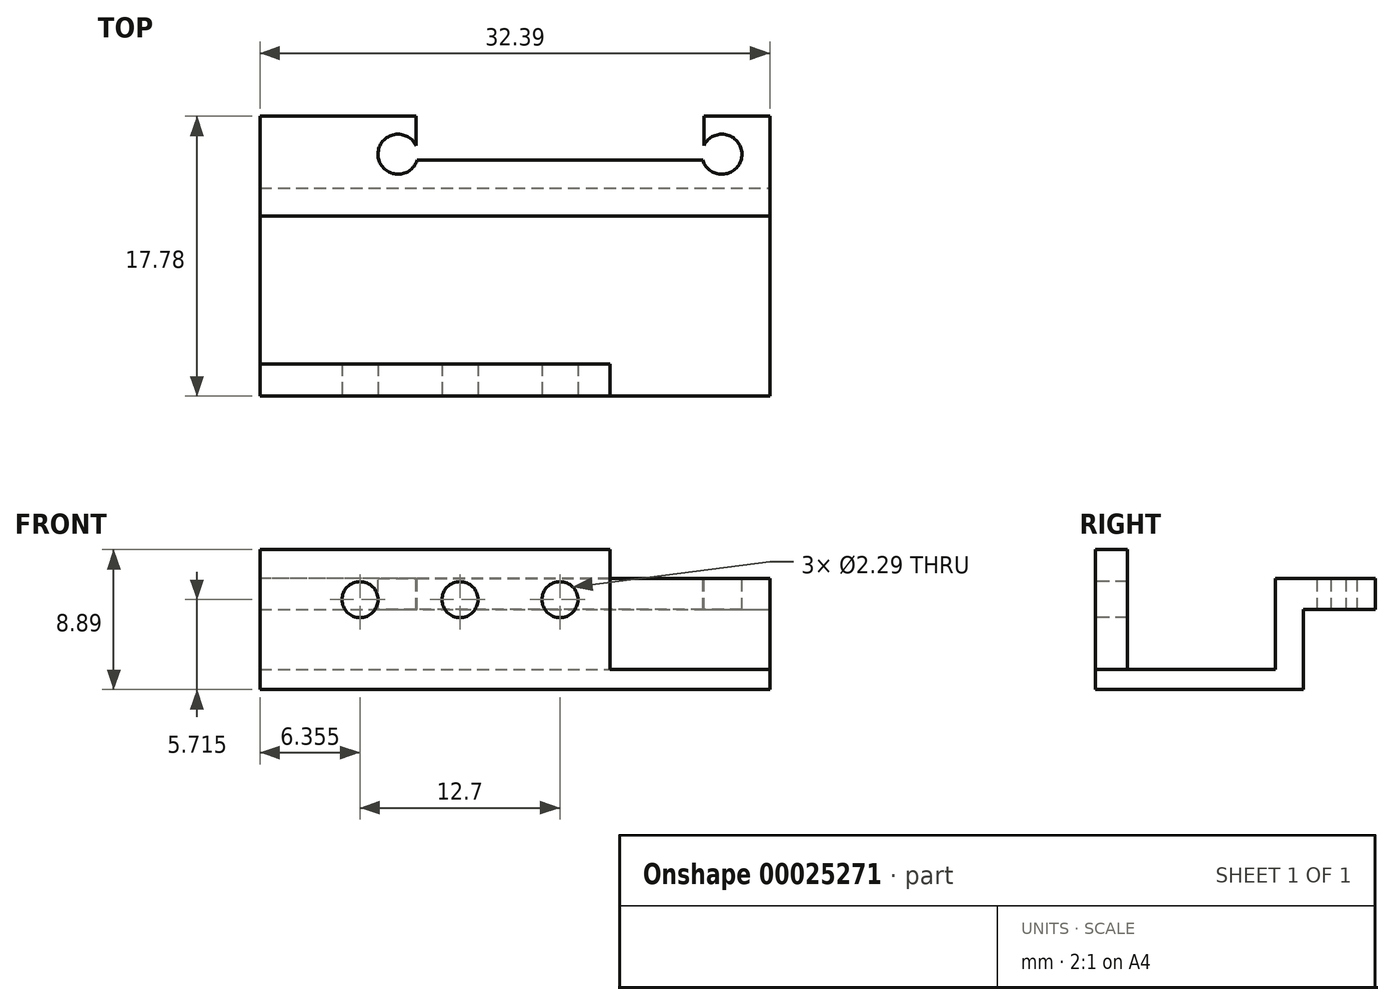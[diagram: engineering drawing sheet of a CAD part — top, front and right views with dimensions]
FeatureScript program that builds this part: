
annotation { "Feature Type Name" : "Feature", "Feature Type Description" : "" }
export const myFeature = defineFeature(function(context is Context, id is Id, definition is map)
    precondition{}
    {
        {
            var Q0;
            Q0=qCreatedBy(makeId("Front.planeOp"),FACE);
            var sketch = newSketch(context, id + "F0", { "sketchPlane" : qUnion([Q0])});
            skLineSegment(sketch, "E0.bottom", {"start": v(0, 0) * mm, "end": v(-22.23, 0) * mm});
            skLineSegment(sketch, "E0.top", {"start": v(0, 8.9) * mm, "end": v(-22.23, 8.89) * mm});
            skLineSegment(sketch, "E0.left", {"start": v(0, 0) * mm, "end": v(0, 8.9) * mm});
            skLineSegment(sketch, "E0.right", {"start": v(-22.23, 0) * mm, "end": v(-22.23, 8.89) * mm});
            skCircle(sketch, "E1", {"center": v(-3.18, 5.72) * mm, "radius": 1.14 * mm});
            skCircle(sketch, "E2", {"center": v(-9.53, 5.71) * mm, "radius": 1.14 * mm});
            skCircle(sketch, "E3", {"center": v(-15.88, 5.71) * mm, "radius": 1.14 * mm});
            skLineSegment(sketch, "E4.bottom", {"start": v(-22.23, 0) * mm, "end": v(15.88, 0) * mm, "construction": true});
            skLineSegment(sketch, "E4.top", {"start": v(-22.23, 38.1) * mm, "end": v(15.87, 38.1) * mm, "construction": true});
            skLineSegment(sketch, "E4.left", {"start": v(-22.23, 0) * mm, "end": v(-22.23, 38.1) * mm, "construction": true});
            skLineSegment(sketch, "E4.right", {"start": v(15.88, 0) * mm, "end": v(15.87, 38.1) * mm, "construction": true});
            skLineSegment(sketch, "E5", {"start": v(-22.23, 19.05) * mm, "end": v(15.87, 19.05) * mm, "construction": true});
            skLineSegment(sketch, "E6", {"start": v(-3.18, 38.1) * mm, "end": v(-3.18, 19.05) * mm, "construction": true});
            skCircle(sketch, "E7", {"center": v(-3.18, 19.05) * mm, "radius": 7.05 * mm, "construction": true});
            skPoint(sketch, "E8.trimOffspring.end.orphan", {"position": v(-3.18, 0) * mm});
            skCircle(sketch, "E9", {"center": v(-3.18, 19.05) * mm, "radius": 6 * mm, "construction": true});
            skLineSegment(sketch, "E10.rect.bottom", {"start": v(11.37, 33.65) * mm, "end": v(-17.72, 33.66) * mm, "construction": true});
            skLineSegment(sketch, "E10.rect.top", {"start": v(11.37, 4.45) * mm, "end": v(-17.72, 4.45) * mm, "construction": true});
            skLineSegment(sketch, "E10.rect.left", {"start": v(11.37, 33.65) * mm, "end": v(11.37, 4.44) * mm, "construction": true});
            skLineSegment(sketch, "E10.rect.right", {"start": v(-17.72, 33.65) * mm, "end": v(-17.72, 4.45) * mm, "construction": true});
            skSolve(sketch);
        }
        {
            var Q0;
            Q0=makeQuery(id+"F0.imprint","IMPRINT",FACE,{"disambiguationData":[TD([[makeQuery(id+"F0.imprint","IMPRINT",EDGE,{"derivedFrom":sQuery(id+"F0.wireOp",EDGE,"E0.bottom")}),-1.0]])]});
            extrude(context, id + "F1", {"entities" : qUnion([Q0]), "oppositeDirection" : true, "depth" : 2.03 * mm});
        }
        {
            var Q0;
            Q0=qCreatedBy(makeId("Right.planeOp"),FACE);
            var sketch = newSketch(context, id + "F2", { "sketchPlane" : qUnion([Q0])});
            skLineSegment(sketch, "E11.bottom", {"start": v(0, 0) * mm, "end": v(17.78, 0) * mm});
            skLineSegment(sketch, "E11.top", {"start": v(0, 1.27) * mm, "end": v(17.78, 1.27) * mm});
            skLineSegment(sketch, "E11.left", {"start": v(0, 0) * mm, "end": v(0, 1.27) * mm});
            skLineSegment(sketch, "E11.right", {"start": v(17.78, 0) * mm, "end": v(17.78, 1.27) * mm});
            skSolve(sketch);
        }
        {
            var Q0;
            Q0=makeQuery(id+"F2.imprint","IMPRINT",FACE,{"disambiguationData":[TD([[makeQuery(id+"F2.imprint","IMPRINT",EDGE,{"derivedFrom":sQuery(id+"F2.wireOp",EDGE,"E11.bottom")}),1.0]])]});
            var Q1;
            Q1=makeQuery(id+"F1.opExtrude","SWEPT_FACE",FACE,{"disambiguationData":[OSD([sQuery(id+"F0.wireOp",EDGE,"E0.right")])]});
            extrude(context, id + "F3", {"entities" : qUnion([Q0]), "operationType" : NewBodyOperationType.ADD, "endBound" : BoundingType.UP_TO_SURFACE, "oppositeDirection" : true, "endBoundEntityFace" : qUnion([Q1]), "depth" : 25.4 * mm});
        }
        {
            var Q0;
            Q0 = qSketchRegion(id + "F2", true);
            extrude(context, id + "F4", {"entities" : qUnion([Q0]), "operationType" : NewBodyOperationType.ADD, "depth" : 10.16 * mm});
        }
        {
            var Q0;
            Q0=makeQuery(id+"F3.boolean.opBoolean","MERGE",FACE,{"derivedFrom":[makeQuery(id+"F1.opExtrude","SWEPT_FACE",FACE,{"disambiguationData":[OSD([sQuery(id+"F0.wireOp",EDGE,"E0.right")])]}),makeQuery(id+"F3.opExtrude","CAP_FACE",FACE,{"disambiguationData":[OSD([sQuery(id+"F2.wireOp",EDGE,"E11.bottom"),sQuery(id+"F2.wireOp",EDGE,"E11.top"),sQuery(id+"F2.wireOp",EDGE,"E11.left"),sQuery(id+"F2.wireOp",EDGE,"E11.right")])],"isStart":false})]});
            var sketch = newSketch(context, id + "F5", { "sketchPlane" : qUnion([Q0])});
            skLineSegment(sketch, "E12.bottom", {"start": v(-17.78, 0) * mm, "end": v(-11.43, 0) * mm});
            skLineSegment(sketch, "E12.top", {"start": v(-17.78, 7.05) * mm, "end": v(-11.43, 7.05) * mm});
            skLineSegment(sketch, "E12.left", {"start": v(-17.78, 0) * mm, "end": v(-17.78, 7.05) * mm});
            skLineSegment(sketch, "E12.right", {"start": v(-11.43, 0) * mm, "end": v(-11.43, 7.05) * mm});
            skSolve(sketch);
        }
        {
            var Q0;
            {var subQ0=sQuery(id+"F2.wireOp",EDGE,"E11.top");Q0=makeQuery(id+"F4.boolean.opBoolean","MERGE",FACE,{"derivedFrom":[makeQuery(id+"F3.opExtrude","SWEPT_FACE",FACE,{"disambiguationData":[OSD([subQ0])]}),makeQuery(id+"F4.opExtrude","SWEPT_FACE",FACE,{"disambiguationData":[OSD([subQ0])]})]});}
            var sketch = newSketch(context, id + "F6", { "sketchPlane" : qUnion([Q0])});
            skLineSegment(sketch, "E13.bottom", {"start": v(5.97, 17.78) * mm, "end": v(-12.32, 17.78) * mm});
            skLineSegment(sketch, "E13.top", {"start": v(5.97, 14.99) * mm, "end": v(-12.32, 14.99) * mm});
            skLineSegment(sketch, "E13.left", {"start": v(5.97, 17.78) * mm, "end": v(5.97, 14.99) * mm});
            skLineSegment(sketch, "E13.right", {"start": v(-12.32, 17.78) * mm, "end": v(-12.32, 14.99) * mm});
            skLineSegment(sketch, "E14", {"start": v(-3.18, 19.13) * mm, "end": v(-3.18, 0) * mm, "construction": true});
            skSolve(sketch);
        }
        {
            var Q0;
            Q0 = qSketchRegion(id + "F5", true);
            var Q1;
            Q1=makeQuery(id+"F4.opExtrude","CAP_FACE",FACE,{"disambiguationData":[OSD([sQuery(id+"F2.wireOp",EDGE,"E11.bottom"),sQuery(id+"F2.wireOp",EDGE,"E11.top"),sQuery(id+"F2.wireOp",EDGE,"E11.left"),sQuery(id+"F2.wireOp",EDGE,"E11.right")])],"isStart":false});
            extrude(context, id + "F7", {"entities" : qUnion([Q0]), "operationType" : NewBodyOperationType.ADD, "endBound" : BoundingType.UP_TO_SURFACE, "oppositeDirection" : true, "endBoundEntityFace" : qUnion([Q1]), "depth" : 25.4 * mm});
        }
        {
            var Q0;
            Q0 = qSketchRegion(id + "F6", true);
            var Q1;
            {var subQ0=sQuery(id+"F2.wireOp",EDGE,"E11.bottom");Q1=makeQuery(id+"F4.boolean.opBoolean","MERGE",FACE,{"derivedFrom":[makeQuery(id+"F3.boolean.opBoolean","MERGE",FACE,{"derivedFrom":[makeQuery(id+"F1.opExtrude","SWEPT_FACE",FACE,{"disambiguationData":[OSD([sQuery(id+"F0.wireOp",EDGE,"E0.bottom")])]}),makeQuery(id+"F3.opExtrude","SWEPT_FACE",FACE,{"disambiguationData":[OSD([subQ0])]})]}),makeQuery(id+"F4.opExtrude","SWEPT_FACE",FACE,{"disambiguationData":[OSD([subQ0])]})]});}
            extrude(context, id + "F8", {"entities" : qUnion([Q0]), "operationType" : NewBodyOperationType.REMOVE, "endBound" : BoundingType.SYMMETRIC, "oppositeDirection" : true, "endBoundEntityFace" : qUnion([Q1]), "depth" : 25.4 * mm});
        }
        {
            var Q0;
            Q0=makeQuery(id+"F7.opExtrude","SWEPT_FACE",FACE,{"disambiguationData":[OSD([sQuery(id+"F5.wireOp",EDGE,"E12.top")])]});
            var sketch = newSketch(context, id + "F9", { "sketchPlane" : qUnion([Q0])});
            skCircle(sketch, "E15", {"center": v(-13.46, 15.37) * mm, "radius": 1.27 * mm});
            skCircle(sketch, "E16", {"center": v(7.11, 15.37) * mm, "radius": 1.27 * mm});
            skSolve(sketch);
        }
        {
            var Q0;
            Q0 = qSketchRegion(id + "F9", true);
            extrude(context, id + "F10", {"entities" : qUnion([Q0]), "operationType" : NewBodyOperationType.REMOVE, "oppositeDirection" : true, "depth" : 25.4 * mm});
        }
        {
            var Q0;
            {var subQ0=sQuery(id+"F2.wireOp",EDGE,"E11.bottom");Q0=makeQuery(id+"F4.boolean.opBoolean","MERGE",FACE,{"derivedFrom":[makeQuery(id+"F3.boolean.opBoolean","MERGE",FACE,{"derivedFrom":[makeQuery(id+"F1.opExtrude","SWEPT_FACE",FACE,{"disambiguationData":[OSD([sQuery(id+"F0.wireOp",EDGE,"E0.bottom")])]}),makeQuery(id+"F3.opExtrude","SWEPT_FACE",FACE,{"disambiguationData":[OSD([subQ0])]})]}),makeQuery(id+"F4.opExtrude","SWEPT_FACE",FACE,{"disambiguationData":[OSD([subQ0])]})]});}
            var sketch = newSketch(context, id + "F11", { "sketchPlane" : qUnion([Q0])});
            skLineSegment(sketch, "E17.bottom", {"start": v(-22.23, -17.78) * mm, "end": v(10.16, -17.78) * mm});
            skLineSegment(sketch, "E17.top", {"start": v(-22.23, -13.2) * mm, "end": v(10.16, -13.2) * mm});
            skLineSegment(sketch, "E17.left", {"start": v(-22.23, -17.78) * mm, "end": v(-22.23, -13.2) * mm});
            skLineSegment(sketch, "E17.right", {"start": v(10.16, -17.78) * mm, "end": v(10.16, -13.2) * mm});
            skSolve(sketch);
        }
        {
            var Q0;
            Q0=makeQuery(id+"F11.imprint","IMPRINT",FACE,{"disambiguationData":[TD([[makeQuery(id+"F11.imprint","IMPRINT",EDGE,{"derivedFrom":sQuery(id+"F11.wireOp",EDGE,"E17.top")}),-1.0]])]});
            extrude(context, id + "F12", {"entities" : qUnion([Q0]), "operationType" : NewBodyOperationType.REMOVE, "oppositeDirection" : true, "depth" : 5.08 * mm});
        }
    });
